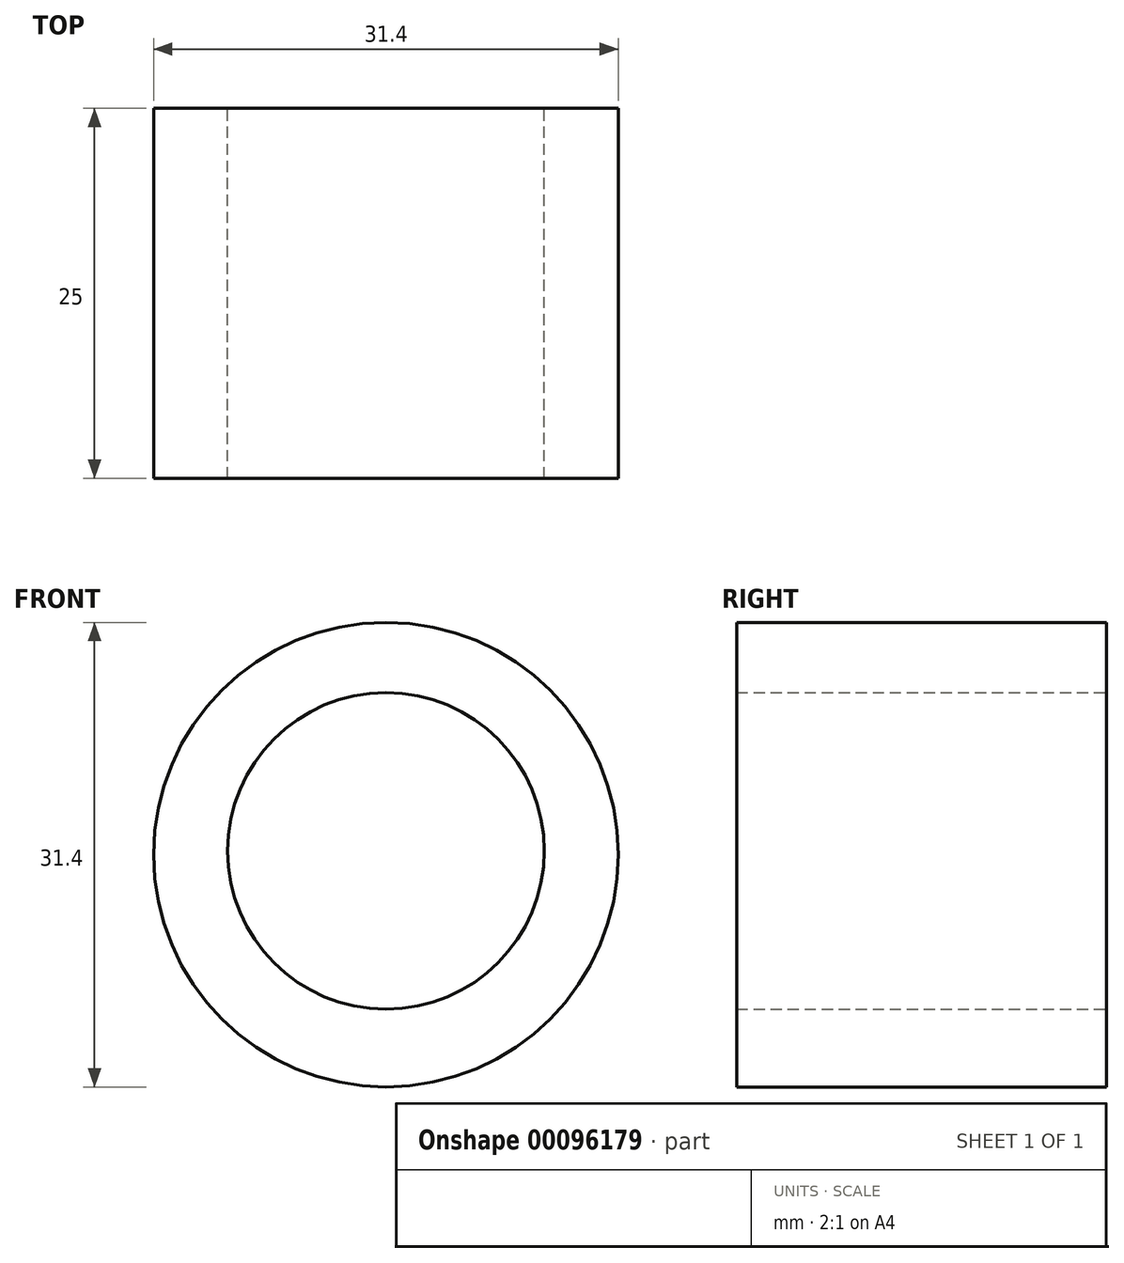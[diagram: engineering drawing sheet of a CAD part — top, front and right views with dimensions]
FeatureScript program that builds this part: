
annotation { "Feature Type Name" : "Feature", "Feature Type Description" : "" }
export const myFeature = defineFeature(function(context is Context, id is Id, definition is map)
    precondition{}
    {
        {
            var Q0;
            Q0=qCreatedBy(makeId("Front.planeOp"),FACE);
            var sketch = newSketch(context, id + "F0", { "sketchPlane" : qUnion([Q0])});
            skCircle(sketch, "E0", {"center": v(-56.96, -22.7) * mm, "radius": 10.7 * mm});
            skCircle(sketch, "E1", {"center": v(-56.96, -22.95) * mm, "radius": 15.7 * mm});
            skSolve(sketch);
        }
        {
            var Q0;
            Q0 = qSketchRegion(id + "F0", true);
            extrude(context, id + "F1", {"entities" : qUnion([Q0]), "depth" : 25 * mm});
        }
    });
